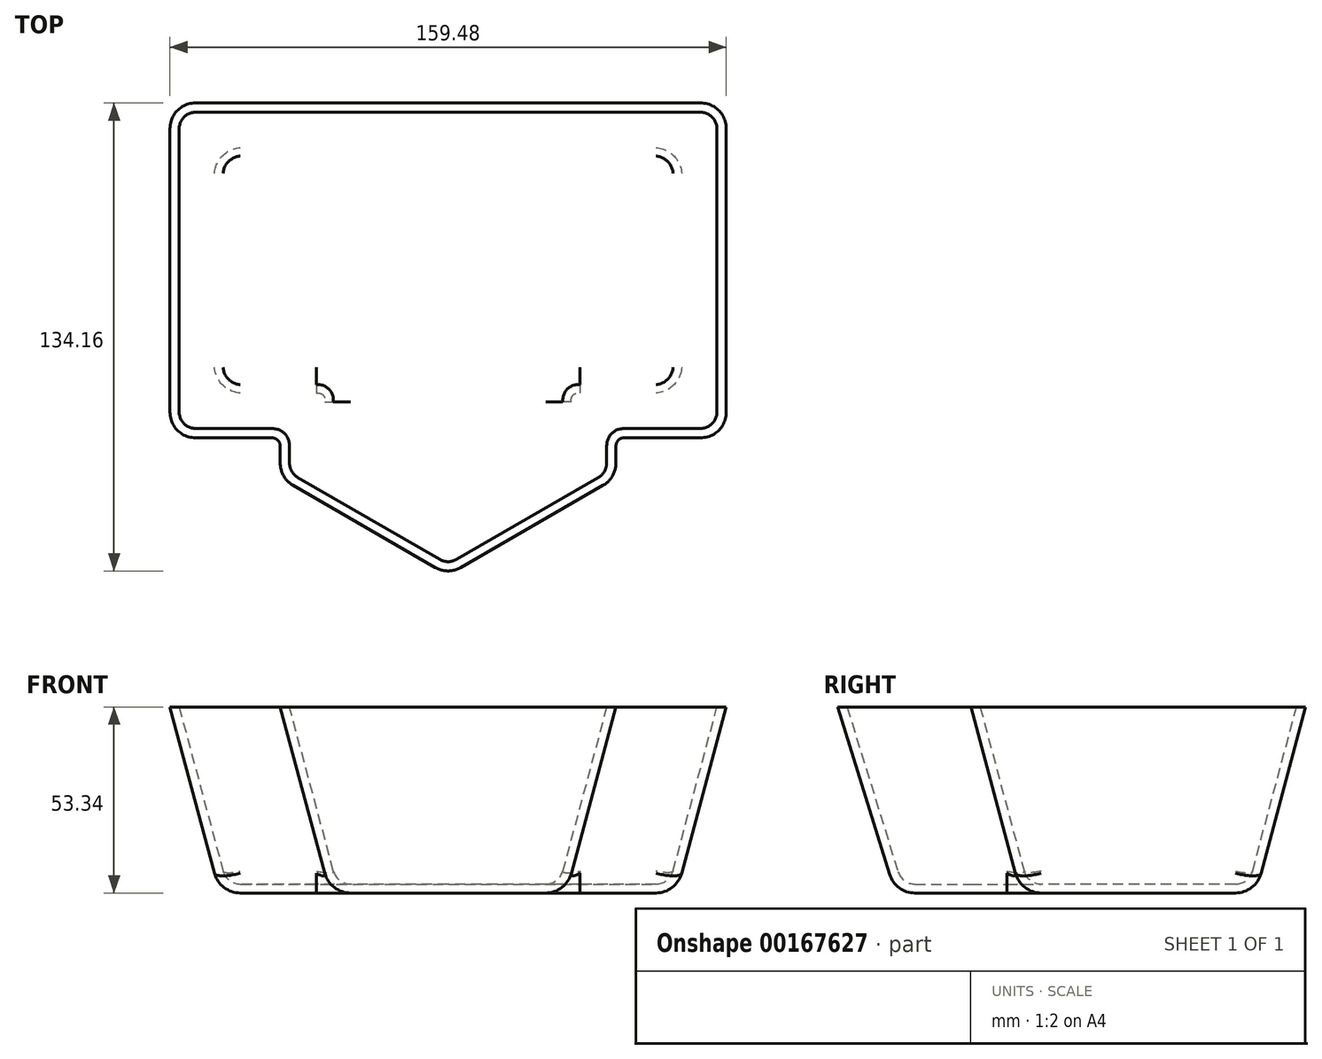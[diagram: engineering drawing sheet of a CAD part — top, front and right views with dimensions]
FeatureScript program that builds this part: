
annotation { "Feature Type Name" : "Feature", "Feature Type Description" : "" }
export const myFeature = defineFeature(function(context is Context, id is Id, definition is map)
    precondition{}
    {
        {
            var Q0;
            Q0=qCreatedBy(makeId("Top.planeOp"),FACE);
            var sketch = newSketch(context, id + "F0", { "sketchPlane" : qUnion([Q0])});
            skLineSegment(sketch, "E0.bottom", {"start": v(0, 0) * mm, "end": v(31.63, 0) * mm});
            skLineSegment(sketch, "E0.top", {"start": v(0, 63.5) * mm, "end": v(127, 63.5) * mm});
            skLineSegment(sketch, "E0.left", {"start": v(0, 0) * mm, "end": v(0, 63.5) * mm});
            skLineSegment(sketch, "E0.right", {"start": v(127, 0) * mm, "end": v(127, 63.5) * mm});
            skCircle(sketch, "E1.cCircle", {"center": v(63.5, 0) * mm, "radius": 36.8 * mm, "construction": true});
            skPoint(sketch, "E1.cCircle.perimeterSnap0", {"position": v(63.5, 0) * mm});
            skLineSegment(sketch, "E1.0", {"start": v(63.5, -36.8) * mm, "end": v(31.63, -18.4) * mm});
            skPoint(sketch, "E1.0.startSnap0", {"position": v(63.5, 0) * mm});
            skLineSegment(sketch, "E1.1", {"start": v(31.63, -18.4) * mm, "end": v(31.63, 0) * mm});
            skLineSegment(sketch, "E1.4", {"start": v(95.37, 0) * mm, "end": v(95.37, -18.4) * mm});
            skLineSegment(sketch, "E1.5", {"start": v(95.37, -18.4) * mm, "end": v(63.5, -36.8) * mm});
            skPoint(sketch, "E2.orphan", {"position": v(95.37, 18.4) * mm});
            skLineSegment(sketch, "E3.trimOffspring", {"start": v(95.37, 0) * mm, "end": v(127, 0) * mm});
            skSolve(sketch);
        }
        {
            var Q0;
            Q0 = qSketchRegion(id + "F0", true);
            extrude(context, id + "F1", {"entities" : qUnion([Q0]), "depth" : 50.8 * mm, "hasDraft" : true, "draftAngle" : 15 * degree});
        }
        {
            var Q0;
            Q0=makeQuery(id+"F1.opExtrude","SWEPT_EDGE",EDGE,{"disambiguationData":[OSD([sQuery(id+"F0.wireOp",EDGE,"E0.bottom"),sQuery(id+"F0.wireOp",EDGE,"E0.right")])]});
            var Q1;
            Q1=makeQuery(id+"F1.opExtrude","SWEPT_EDGE",EDGE,{"disambiguationData":[OSD([sQuery(id+"F0.wireOp",EDGE,"E0.bottom"),sQuery(id+"F0.wireOp",EDGE,"E0.left")])]});
            var Q2;
            Q2=makeQuery(id+"F1.opExtrude","SWEPT_EDGE",EDGE,{"disambiguationData":[OSD([sQuery(id+"F0.wireOp",EDGE,"E0.top"),sQuery(id+"F0.wireOp",EDGE,"E0.right")])]});
            var Q3;
            Q3=makeQuery(id+"F1.opExtrude","SWEPT_EDGE",EDGE,{"disambiguationData":[OSD([sQuery(id+"F0.wireOp",EDGE,"E0.top"),sQuery(id+"F0.wireOp",EDGE,"E0.left")])]});
            var Q4;
            Q4=makeQuery(id+"F1.opExtrude","SWEPT_EDGE",EDGE,{"disambiguationData":[OSD([sQuery(id+"F0.wireOp",EDGE,"E1.0"),sQuery(id+"F0.wireOp",EDGE,"E1.5")])]});
            var Q5;
            Q5=makeQuery(id+"F1.opExtrude","SWEPT_EDGE",EDGE,{"disambiguationData":[OSD([sQuery(id+"F0.wireOp",EDGE,"E1.4"),sQuery(id+"F0.wireOp",EDGE,"E1.5")])]});
            var Q6;
            Q6=makeQuery(id+"F1.opExtrude","SWEPT_EDGE",EDGE,{"disambiguationData":[OSD([sQuery(id+"F0.wireOp",EDGE,"E1.4"),sQuery(id+"F0.wireOp",EDGE,"E3.trimOffspring")])]});
            var Q7;
            Q7=makeQuery(id+"F1.opExtrude","SWEPT_EDGE",EDGE,{"disambiguationData":[OSD([sQuery(id+"F0.wireOp",EDGE,"E1.0"),sQuery(id+"F0.wireOp",EDGE,"E1.1")])]});
            fillet(context, id + "F2", {"entities" : qUnion([Q0, Q1, Q2, Q3, Q4, Q5, Q6, Q7]), "radius" : 5.08 * mm, "tangentPropagation" : true, "allowEdgeOverflow" : false});
        }
        {
            var Q0;
            Q0=makeQuery(id+"F1.opExtrude","CAP_EDGE",EDGE,{"disambiguationData":[OSD([sQuery(id+"F0.wireOp",EDGE,"E0.bottom")])],"isStart":true});
            fillet(context, id + "F3", {"entities" : qUnion([Q0]), "radius" : 5.08 * mm, "tangentPropagation" : true, "allowEdgeOverflow" : false});
        }
        {
            var Q0;
            Q0=makeQuery(id+"F1.opExtrude","CAP_FACE",FACE,{"disambiguationData":[OSD([sQuery(id+"F0.wireOp",EDGE,"E0.bottom"),sQuery(id+"F0.wireOp",EDGE,"E0.top"),sQuery(id+"F0.wireOp",EDGE,"E0.left"),sQuery(id+"F0.wireOp",EDGE,"E0.right")])],"isStart":false});
            shell(context, id + "F4", {"entities" : qUnion([Q0]), "thickness" : 2.54 * mm, "oppositeDirection" : true});
        }
    });
